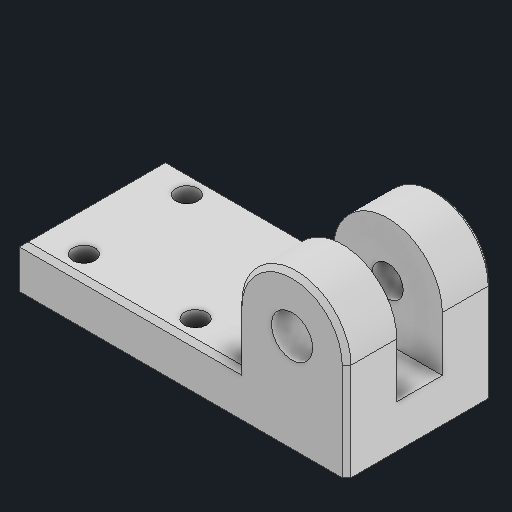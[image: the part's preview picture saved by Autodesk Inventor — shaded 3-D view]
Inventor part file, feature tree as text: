
AUTODESK INVENTOR PART (.ipt)
format: ipt  version: 2025.1 (Build 291241020, 241B)  size: 180,224 bytes
history: native  units: in
note: dims shown in document units (in); Inventor stores cm internally (conversion verified against a paired STEP export)
features: sketch x3, extrude x3, hole x3, projected_geometry x2, fillet x1, chamfer x1
ambient origin geometry x8: Origin, YZ Plane, XZ Plane, XY Plane, X Axis, Y Axis, Z Axis, Center Point
bodies: Solid1 (feature_tree)
feature tree (13):
  sketch  "Sketch1"  dims[d0=1.5in d1=0.6693in]
  extrude  "Extrusion1"  Depth=0.6693in
  sketch  "Sketch2"  dims[d4=0.1969in d5=0.0in d6=0.5in]
  extrude  "Extrusion2"  Depth=0.5in
  extrude  "Extrusion3"  TaperAngle=0.0deg  [1 undecoded]
  hole  "Hole1"  [1 undecoded]
  fillet  "Fillet1"  Radius=1.0in
  chamfer  "Chamfer1"  Distance=0.25in
  hole  "Hole2"  [1 undecoded]
  hole  "Hole3"  [1 undecoded]
  projected_geometry  "Projected Loop1"
  sketch  "Sketch3"  dims[d7=0.5in d8=0.0in d9=0.0in d10=0.2087in d11=1.0in d12=0.0in d13=0.25in d14=0.1181in d15=0.02in d16=0.125in d17=45.0deg d20=0.102in d21=0.75in d22=0.248in d23=0.25in d24=90.0deg d25=1.0in d26=0.8108in d27=0.142in d28=0.75in d29=0.375in d30=0.25in d31=0.5635in d32=1.0in d33=0.8108in d34=0.189in d35=0.75in d36=0.37in d37=0.25in d38=90.0deg d39=1.0in d40=0.8108in d41=0.0787in d42=0.0787in d43=0.0787in d44=0.0787in d45=0.5118in d46=0.4724in d47=0.0985in d48=0.1969in]
  projected_geometry  "Projected Loop2"
note: 4 required parameter values undecoded (feature->parameter linkage not recoverable at this tier; creation-order binding heuristic only, values carry confidence <= 0.55)
